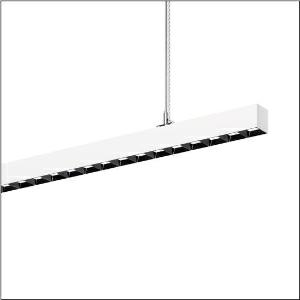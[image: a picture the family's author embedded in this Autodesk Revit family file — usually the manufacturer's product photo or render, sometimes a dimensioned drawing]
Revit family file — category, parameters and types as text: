
# Revit family: silica_r__21_51mx32tctdw_3fbf
name_source: partatom
category: Lighting Fixtures
units: mm (PartAtom-declared; Revit-internal decimal feet)

## family parameters
Cut with Voids When Loaded = No
Host = Face
Light Source = No
Part Type = Normal
Room Calculation Point = No
Round Connector Dimension = Use Diameter
Shared = No

## types (1)
- --- (1 x LED, 15540 lm, 133.6 W, 6500K)
    Apparent Load = 134 VA
    CIE Flux Codes = 84 99 100 60 100
    Color Rendering = 80
    Color Temperature = 6500K
    Default Elevation = 1800 mm
    Description = Silica® 21, office luminaire, primary light control with darklight reflector, of PMMA, black, CAT 2 (L<= 3000cd/m²), light emission: direct/indirect distribution, primary light characteristic: symmetric, installation type: suspended mounting, LED, rated luminous flux: 15.540lm, luminous efficacy: 111lm/W, light colour: 8tw, colour temperature: 2700..6500K, control gear: ECG DALI, with terminal, 3+2-pole, max. 2.5mm², mains connection: 220..240V, AC, 50/60Hz, rated input power: 140.3W, luminaire housing, of aluminium, traffic white (RAL 9016), length: 3.004mm, width: 53mm, height: 53mm, protection rating (complete): IP20, insulation class (complete): insulation class I (protective earthing), certification: CE, permissible operating ambient temperature: 0..+35°C, standard: EN 50419, packaging unit: 1 piece
    Height = 53 mm
    Lamp = 1 x LED
    Lamp Light Flux = 15540 lm
    Lamp Power = 133.6 W
    Lamp count = 1
    Length = 3004 mm
    Luminous efficacy = 116 lm/W
    Manufacturer = Siteco
    ModVariant = No
    Model = 51MX32TCTDW
    Mounting Place = Ceiling
    Mounting Type = Pendant
    Number of Poles = 1
    OnlyDefault = Yes
    Power Factor = 1
    Product Name = Silica® 21
    Product group = office luminaire | ceiling pendant
    ProductGroupID = 902
    Protection Class = Protection class I
    Protection Degree = IP 20
    RLX_Detail_Level = 1
    RLX_Emergency_Light_Flux = 0 lm
    RLX_Emergency_Type = 0
    RLX_Emergency_Type_DB = No
    RlxData = <blob elided: 61057 chars, md5=a6173e9c>
    Socket = socket
    Standby Power = 0 W
    System Light Flux = 15540 lm
    System Power = 134 W
    Type Comments = individual setting
    Type Image = l_1297801.jpg
    URL = http://relux.com
    VarID = @adj_071275
    Voltage = 0 V
    Weight = 0.00 kg
    Width = 53 mm

## geometry (parser evidence)
native form markers: Blend x4, Sweep x13
no freeform markers — native parametric forms only
